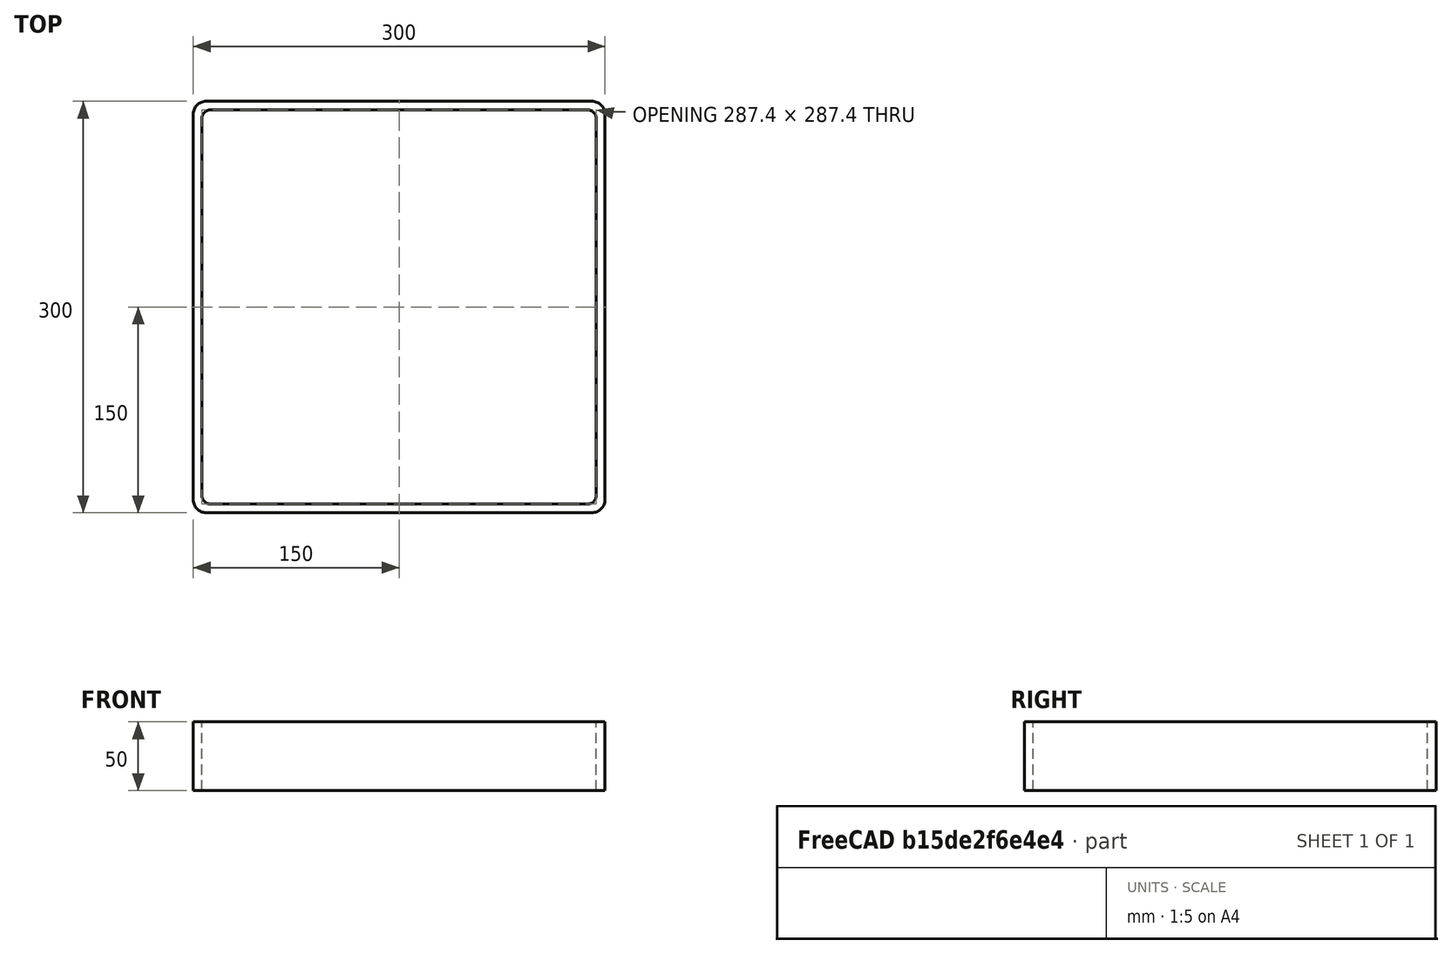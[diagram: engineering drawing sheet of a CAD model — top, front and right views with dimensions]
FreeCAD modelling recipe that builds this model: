
FCSTD DOCUMENT  (FreeCAD 0.15R4671 (Git))
Label: Square hollow section 300x300x6.3 EN10219 S235JRH
License: All rights reserved
LicenseURL: http://en.wikipedia.org/wiki/All_rights_reserved
objects: Sketcher::SketchObject×1, Part::Extrusion×1
note: 2 computed .brp shape members not serialized (recipe doc carries the construction recipe); baked Part::Feature solids carry a one-line shape summary decoded from their .brp

FEATURE [Sketcher::SketchObject] Sketch
  sketch-geometry (16):
    g0: LineSegment StartX=-137.4 StartY=143.7 StartZ=0 EndX=137.4 EndY=143.7 EndZ=0
    g1: LineSegment StartX=143.7 StartY=137.4 StartZ=0 EndX=143.7 EndY=-137.4 EndZ=0
    g2: LineSegment StartX=137.4 StartY=-143.7 StartZ=0 EndX=-137.4 EndY=-143.7 EndZ=0
    g3: LineSegment StartX=-143.7 StartY=-137.4 StartZ=0 EndX=-143.7 EndY=137.4 EndZ=0
    g4: LineSegment StartX=-140.55 StartY=150 StartZ=0 EndX=140.55 EndY=150 EndZ=0
    g5: LineSegment StartX=150 StartY=140.55 StartZ=0 EndX=150 EndY=-140.55 EndZ=0
    g6: LineSegment StartX=140.55 StartY=-150 StartZ=0 EndX=-140.55 EndY=-150 EndZ=0
    g7: LineSegment StartX=-150 StartY=-140.55 StartZ=0 EndX=-150 EndY=140.55 EndZ=0
    g8: ArcOfCircle CenterX=-137.4 CenterY=137.4 CenterZ=0 NormalX=0 NormalY=0 NormalZ=1 Radius=6.3 StartAngle=1.5708 EndAngle=3.14159
    g9: ArcOfCircle CenterX=137.4 CenterY=137.4 CenterZ=0 NormalX=0 NormalY=0 NormalZ=1 Radius=6.3 StartAngle=0 EndAngle=1.5708
    g10: ArcOfCircle CenterX=137.4 CenterY=-137.4 CenterZ=0 NormalX=0 NormalY=0 NormalZ=1 Radius=6.3 StartAngle=4.71239 EndAngle=6.28319
    g11: ArcOfCircle CenterX=-137.4 CenterY=-137.4 CenterZ=0 NormalX=0 NormalY=0 NormalZ=1 Radius=6.3 StartAngle=3.14159 EndAngle=4.71239
    g12: ArcOfCircle CenterX=140.55 CenterY=140.55 CenterZ=0 NormalX=0 NormalY=0 NormalZ=1 Radius=9.45 StartAngle=0 EndAngle=1.5708
    g13: ArcOfCircle CenterX=140.55 CenterY=-140.55 CenterZ=0 NormalX=0 NormalY=0 NormalZ=1 Radius=9.45 StartAngle=4.71239 EndAngle=6.28319
    g14: ArcOfCircle CenterX=-140.55 CenterY=-140.55 CenterZ=0 NormalX=0 NormalY=0 NormalZ=1 Radius=9.45 StartAngle=3.14159 EndAngle=4.71239
    g15: ArcOfCircle CenterX=-140.55 CenterY=140.55 CenterZ=0 NormalX=0 NormalY=0 NormalZ=1 Radius=9.45 StartAngle=1.5708 EndAngle=3.14159
  constraints (36):
    c: Horizontal(g2)
    c: Vertical(g3)
    c: Horizontal(g6)
    c: Vertical(g7)
    c: Tangent(g3,g8) = 1.5708
    c: Tangent(g0,g8) = 1.5708
    c: Tangent(g0,g9) = 1.5708
    c: Tangent(g1,g9) = 1.5708
    c: Tangent(g1,g10) = 1.5708
    c: Tangent(g2,g10) = 1.5708
    c: Tangent(g2,g11) = 1.5708
    c: Tangent(g3,g11) = 1.5708
    c: Tangent(g4,g12) = 1.5708
    c: Tangent(g5,g12) = 1.5708
    c: Tangent(g5,g13) = 1.5708
    c: Tangent(g6,g13) = 1.5708
    c: Tangent(g6,g14) = 1.5708
    c: Tangent(g7,g14) = 1.5708
    c: Tangent(g7,g15) = 1.5708
    c: Tangent(g4,g15) = 1.5708
    c: Equal(g9,g8)
    c: Equal(g9,g11)
    c: Equal(g9,g10)
    c: Equal(g12,g15)
    c: Equal(g12,g14)
    c: Equal(g12,g13)
    c: Symmetric(g4,g6,g-1)
    c: Symmetric(g7,g5,g-2)
    c: DistanceY(g4,g6) = -300
    c: DistanceX(g7,g5) = 300
    c: Symmetric(g3,g1,g-2)
    c: Symmetric(g0,g2,g-1)
    c: DistanceY(g0,g4) = 6.3
    c: DistanceX(g5,g1) = -6.3
    c: Radius(g9) = 6.3
    c: Radius(g12) = 9.45
FEATURE [Part::Extrusion] Extrude  label="Square hollow section 300x300x6.3 EN10219 S235JRH"
  Base = -> Sketch
  Dir = (0,0,50)
  Solid = true
